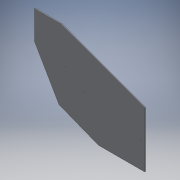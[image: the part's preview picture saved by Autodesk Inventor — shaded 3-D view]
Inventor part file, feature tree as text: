
AUTODESK INVENTOR PART (.ipt)
format: ipt  version: 2018.2 (Build 222227000, 227)  size: 153,600 bytes
history: native  units: mm
features: extrude x5, sketch x5, other x4, reference x4, chamfer x1
ambient origin geometry x8: Origin, YZ Plane, XZ Plane, XY Plane, X Axis, Y Axis, Z Axis, Center Point
bodies: Body1 (feature_tree), Body2 (feature_tree)
feature tree (19):
  other  "ソリッド1"
  extrude  "押し出し1"  Depth=555.0mm
  extrude  "押し出し4"  Depth=555.0mm
  extrude  "押し出し5"  Depth=5.0mm TaperAngle=0.0deg
  chamfer  "面取り2"  Distance=5.0mm
  extrude  "押し出し6"  Depth=5.0mm
  extrude  "押し出し7"  Depth=320.0mm
  sketch  "スケッチ1"
  sketch  "スケッチ3"
  sketch  "スケッチ5"
  reference  "参照1"
  reference  "参照2"
  reference  "参照3"
  reference  "参照4"
  sketch  "スケッチ6"
  sketch  "スケッチ7"
  other  "<userpath>\Documents\Inventor\AeroCAD2018\設計\Rr.wing\model.iam"
  other  "model.iam"
  other  "endplate:1"
